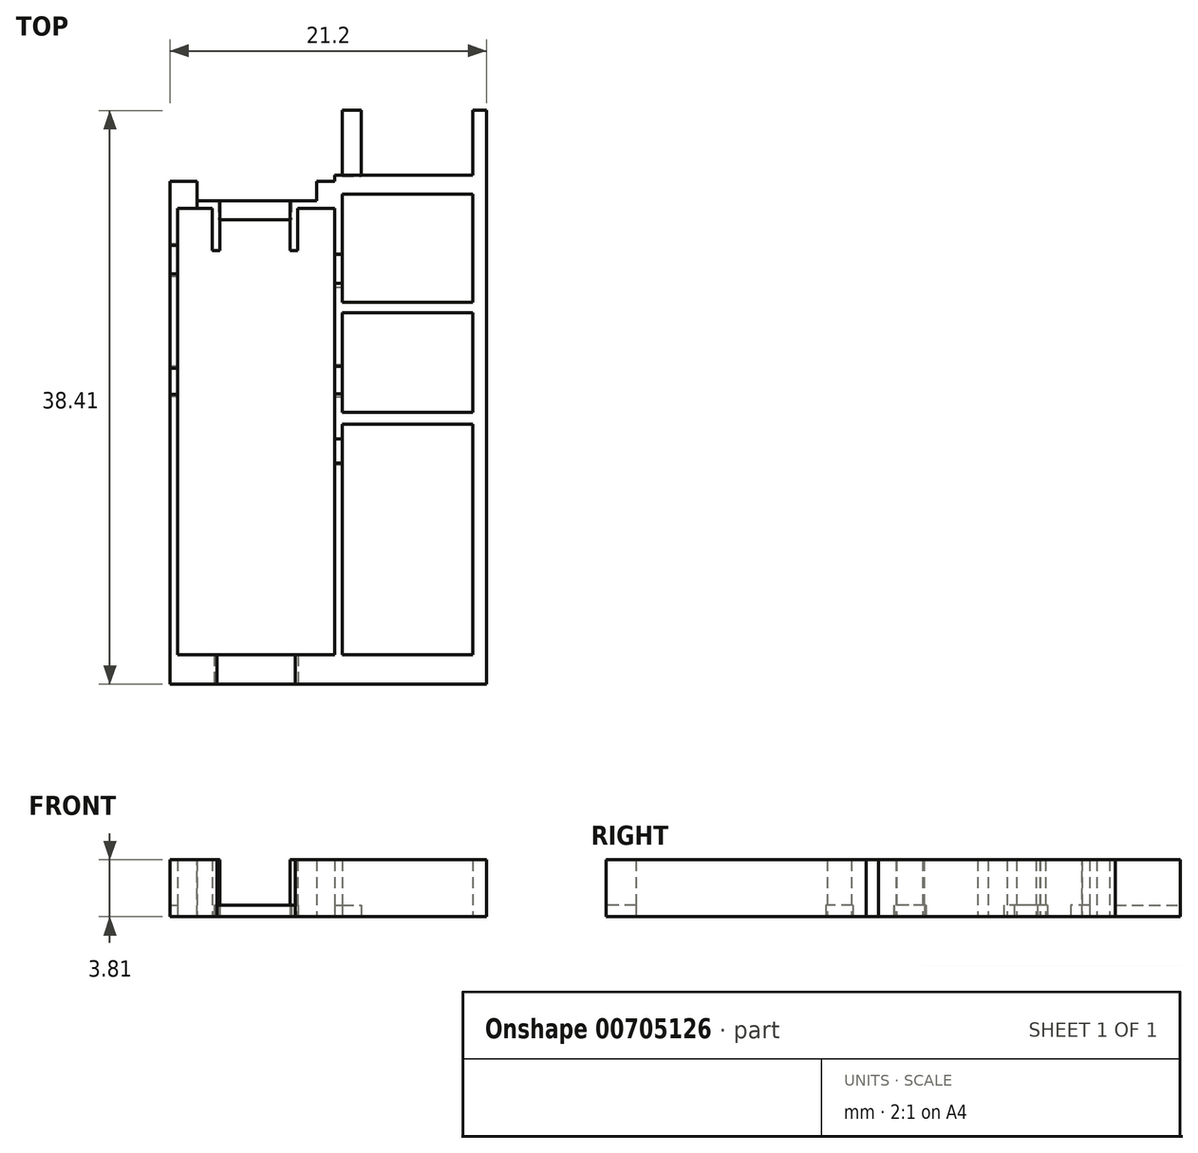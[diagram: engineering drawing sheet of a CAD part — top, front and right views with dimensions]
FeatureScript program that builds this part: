
annotation { "Feature Type Name" : "Feature", "Feature Type Description" : "" }
export const myFeature = defineFeature(function(context is Context, id is Id, definition is map)
    precondition{}
    {
        {
            var Q0;
            Q0=qCreatedBy(makeId("Top.planeOp"),FACE);
            var sketch = newSketch(context, id + "F0", { "sketchPlane" : qUnion([Q0])});
            skLineSegment(sketch, "E0.bottom", {"start": v(19.6, -47.44) * mm, "end": v(20.1, -47.44) * mm});
            skLineSegment(sketch, "E0.top", {"start": v(19.6, -42.13) * mm, "end": v(20.1, -42.13) * mm});
            skLineSegment(sketch, "E0.left", {"start": v(19.6, -47.44) * mm, "end": v(19.6, -42.13) * mm});
            skLineSegment(sketch, "E0.right", {"start": v(20.1, -47.44) * mm, "end": v(20.1, -42.13) * mm});
            skLineSegment(sketch, "E1.bottom", {"start": v(19.6, -49.37) * mm, "end": v(20.1, -49.37) * mm});
            skLineSegment(sketch, "E1.top", {"start": v(19.6, -54.93) * mm, "end": v(20.1, -54.93) * mm});
            skLineSegment(sketch, "E1.left", {"start": v(19.6, -49.37) * mm, "end": v(19.6, -54.93) * mm});
            skLineSegment(sketch, "E1.right", {"start": v(20.1, -49.37) * mm, "end": v(20.1, -54.93) * mm});
            skLineSegment(sketch, "E2.bottom", {"start": v(19.6, -61.4) * mm, "end": v(20.1, -61.4) * mm});
            skLineSegment(sketch, "E2.top", {"start": v(19.6, -74.22) * mm, "end": v(20.1, -74.22) * mm});
            skLineSegment(sketch, "E2.left", {"start": v(19.6, -61.4) * mm, "end": v(19.6, -74.22) * mm});
            skLineSegment(sketch, "E2.right", {"start": v(20.1, -61.4) * mm, "end": v(20.1, -74.22) * mm});
            skLineSegment(sketch, "E3.bottom", {"start": v(19.6, -56.76) * mm, "end": v(20.1, -56.76) * mm});
            skLineSegment(sketch, "E3.top", {"start": v(19.6, -59.79) * mm, "end": v(20.1, -59.79) * mm});
            skLineSegment(sketch, "E3.left", {"start": v(19.6, -56.76) * mm, "end": v(19.6, -59.79) * mm});
            skLineSegment(sketch, "E3.right", {"start": v(20.1, -56.76) * mm, "end": v(20.1, -59.79) * mm});
            skLineSegment(sketch, "E4.bottom", {"start": v(20.1, -58) * mm, "end": v(29.76, -58) * mm});
            skLineSegment(sketch, "E4.top", {"start": v(20.1, -58.8) * mm, "end": v(29.76, -58.8) * mm});
            skLineSegment(sketch, "E4.left", {"start": v(20.1, -58) * mm, "end": v(20.1, -58.8) * mm});
            skLineSegment(sketch, "E4.right", {"start": v(29.76, -58) * mm, "end": v(29.76, -58.8) * mm});
            skLineSegment(sketch, "E5.bottom", {"start": v(20.1, -50.64) * mm, "end": v(29.58, -50.64) * mm});
            skLineSegment(sketch, "E5.top", {"start": v(20.1, -51.34) * mm, "end": v(29.58, -51.34) * mm});
            skLineSegment(sketch, "E5.left", {"start": v(20.1, -50.64) * mm, "end": v(20.1, -51.34) * mm});
            skLineSegment(sketch, "E5.right", {"start": v(29.58, -50.64) * mm, "end": v(29.58, -51.34) * mm});
            skLineSegment(sketch, "E6.bottom", {"start": v(20.1, -42.13) * mm, "end": v(29.74, -42.13) * mm});
            skLineSegment(sketch, "E6.top", {"start": v(20.1, -43.4) * mm, "end": v(29.74, -43.4) * mm});
            skLineSegment(sketch, "E6.left", {"start": v(20.1, -42.13) * mm, "end": v(20.1, -43.4) * mm});
            skLineSegment(sketch, "E6.right", {"start": v(29.74, -42.13) * mm, "end": v(29.74, -43.4) * mm});
            skLineSegment(sketch, "E7.bottom", {"start": v(9.07, -56.8) * mm, "end": v(8.56, -56.8) * mm});
            skLineSegment(sketch, "E7.top", {"start": v(9.07, -74.23) * mm, "end": v(8.56, -74.23) * mm});
            skLineSegment(sketch, "E7.left", {"start": v(9.07, -56.8) * mm, "end": v(9.07, -74.23) * mm});
            skLineSegment(sketch, "E7.right", {"start": v(8.56, -56.8) * mm, "end": v(8.56, -74.23) * mm});
            skLineSegment(sketch, "E8.bottom", {"start": v(9.07, -55.04) * mm, "end": v(8.56, -55.04) * mm});
            skLineSegment(sketch, "E8.top", {"start": v(9.07, -48.74) * mm, "end": v(8.56, -48.74) * mm});
            skLineSegment(sketch, "E8.left", {"start": v(9.07, -55.04) * mm, "end": v(9.07, -48.74) * mm});
            skLineSegment(sketch, "E8.right", {"start": v(8.56, -55.04) * mm, "end": v(8.56, -48.74) * mm});
            skLineSegment(sketch, "E9.bottom", {"start": v(8.57, -42.53) * mm, "end": v(10.38, -42.53) * mm});
            skLineSegment(sketch, "E9.top", {"start": v(8.57, -44.35) * mm, "end": v(10.38, -44.35) * mm});
            skLineSegment(sketch, "E9.left", {"start": v(8.57, -42.53) * mm, "end": v(8.57, -44.35) * mm});
            skLineSegment(sketch, "E9.right", {"start": v(10.38, -42.53) * mm, "end": v(10.38, -44.35) * mm});
            skLineSegment(sketch, "E10.bottom", {"start": v(8.57, -44.35) * mm, "end": v(9.08, -44.35) * mm});
            skLineSegment(sketch, "E10.top", {"start": v(8.57, -46.82) * mm, "end": v(9.08, -46.82) * mm});
            skLineSegment(sketch, "E10.left", {"start": v(8.57, -44.35) * mm, "end": v(8.57, -46.82) * mm});
            skLineSegment(sketch, "E10.right", {"start": v(9.08, -44.35) * mm, "end": v(9.08, -46.82) * mm});
            skLineSegment(sketch, "E11.bottom", {"start": v(10.38, -44.35) * mm, "end": v(11.41, -44.35) * mm});
            skLineSegment(sketch, "E11.top", {"start": v(10.38, -43.84) * mm, "end": v(11.41, -43.84) * mm});
            skLineSegment(sketch, "E11.left", {"start": v(10.38, -44.35) * mm, "end": v(10.38, -43.84) * mm});
            skLineSegment(sketch, "E11.right", {"start": v(11.41, -44.35) * mm, "end": v(11.41, -43.84) * mm});
            skLineSegment(sketch, "E12.bottom", {"start": v(11.41, -43.84) * mm, "end": v(11.92, -43.84) * mm});
            skLineSegment(sketch, "E12.top", {"start": v(11.41, -47.17) * mm, "end": v(11.92, -47.17) * mm});
            skLineSegment(sketch, "E12.left", {"start": v(11.41, -43.84) * mm, "end": v(11.41, -47.17) * mm});
            skLineSegment(sketch, "E12.right", {"start": v(11.92, -43.84) * mm, "end": v(11.92, -47.17) * mm});
            skLineSegment(sketch, "E13.bottom", {"start": v(19.6, -42.53) * mm, "end": v(18.37, -42.53) * mm});
            skLineSegment(sketch, "E13.top", {"start": v(19.6, -44.35) * mm, "end": v(18.37, -44.35) * mm});
            skLineSegment(sketch, "E13.left", {"start": v(19.6, -42.53) * mm, "end": v(19.6, -44.35) * mm});
            skLineSegment(sketch, "E13.right", {"start": v(18.37, -42.53) * mm, "end": v(18.37, -44.35) * mm});
            skLineSegment(sketch, "E14.bottom", {"start": v(18.37, -44.35) * mm, "end": v(17.12, -44.35) * mm});
            skLineSegment(sketch, "E14.top", {"start": v(18.37, -43.84) * mm, "end": v(17.12, -43.84) * mm});
            skLineSegment(sketch, "E14.left", {"start": v(18.37, -44.35) * mm, "end": v(18.37, -43.84) * mm});
            skLineSegment(sketch, "E14.right", {"start": v(17.12, -44.35) * mm, "end": v(17.12, -43.84) * mm});
            skLineSegment(sketch, "E15.bottom", {"start": v(17.12, -43.84) * mm, "end": v(16.6, -43.84) * mm});
            skLineSegment(sketch, "E15.top", {"start": v(17.12, -47.16) * mm, "end": v(16.6, -47.16) * mm});
            skLineSegment(sketch, "E15.left", {"start": v(17.12, -43.84) * mm, "end": v(17.12, -47.16) * mm});
            skLineSegment(sketch, "E15.right", {"start": v(16.6, -43.84) * mm, "end": v(16.6, -47.16) * mm});
            skLineSegment(sketch, "E16.bottom", {"start": v(29.74, -42.13) * mm, "end": v(28.84, -42.13) * mm});
            skLineSegment(sketch, "E16.top", {"start": v(29.74, -76.2) * mm, "end": v(28.84, -76.2) * mm});
            skLineSegment(sketch, "E16.left", {"start": v(29.74, -42.13) * mm, "end": v(29.74, -76.2) * mm});
            skLineSegment(sketch, "E16.right", {"start": v(28.84, -42.13) * mm, "end": v(28.84, -76.2) * mm});
            skLineSegment(sketch, "E17.bottom", {"start": v(28.84, -76.2) * mm, "end": v(16.95, -76.2) * mm});
            skLineSegment(sketch, "E17.top", {"start": v(28.84, -74.22) * mm, "end": v(16.95, -74.22) * mm});
            skLineSegment(sketch, "E17.left", {"start": v(28.84, -76.2) * mm, "end": v(28.84, -74.22) * mm});
            skLineSegment(sketch, "E17.right", {"start": v(16.95, -76.2) * mm, "end": v(16.95, -74.22) * mm});
            skLineSegment(sketch, "E18.bottom", {"start": v(11.71, -76.2) * mm, "end": v(8.56, -76.2) * mm});
            skLineSegment(sketch, "E18.top", {"start": v(11.71, -74.22) * mm, "end": v(8.56, -74.22) * mm});
            skLineSegment(sketch, "E18.left", {"start": v(11.71, -76.2) * mm, "end": v(11.71, -74.22) * mm});
            skLineSegment(sketch, "E18.right", {"start": v(8.56, -76.2) * mm, "end": v(8.56, -74.22) * mm});
            skLineSegment(sketch, "E19.top", {"start": v(29.75, -42.13) * mm, "end": v(28.84, -42.13) * mm});
            skLineSegment(sketch, "E19.left", {"start": v(29.75, -37.79) * mm, "end": v(29.75, -42.13) * mm});
            skLineSegment(sketch, "E19.right", {"start": v(28.84, -37.79) * mm, "end": v(28.84, -42.13) * mm});
            skLineSegment(sketch, "E20", {"start": v(28.84, -37.79) * mm, "end": v(29.75, -37.79) * mm});
            skPoint(sketch, "E21.endSnap0", {"position": v(22.9, -76.2) * mm});
            skLineSegment(sketch, "E22", {"start": v(8.56, -76.2) * mm, "end": v(29.74, -76.2) * mm});
            skSolve(sketch);
        }
        {
            var Q0;
            Q0=qSketchRegion(id+"F0",true);
            extrude(context, id + "F1", {"entities" : qUnion([Q0]), "depth" : 3.8 * mm, "offsetDistance" : 25.4 * mm});
        }
        {
            var Q0;
            Q0=qCreatedBy(makeId("Top.planeOp"),FACE);
            var sketch = newSketch(context, id + "F2", { "sketchPlane" : qUnion([Q0])});
            skLineSegment(sketch, "E23.bottom", {"start": v(11.81, -43.84) * mm, "end": v(16.72, -43.84) * mm});
            skLineSegment(sketch, "E23.top", {"start": v(11.81, -45.11) * mm, "end": v(16.72, -45.11) * mm});
            skLineSegment(sketch, "E23.left", {"start": v(11.81, -43.84) * mm, "end": v(11.81, -45.11) * mm});
            skLineSegment(sketch, "E23.right", {"start": v(16.72, -43.84) * mm, "end": v(16.72, -45.11) * mm});
            skLineSegment(sketch, "E24.bottom", {"start": v(19.6, -54.8) * mm, "end": v(20.1, -54.8) * mm});
            skLineSegment(sketch, "E24.top", {"start": v(19.6, -56.96) * mm, "end": v(20.1, -56.96) * mm});
            skLineSegment(sketch, "E24.left", {"start": v(19.6, -54.8) * mm, "end": v(19.6, -56.96) * mm});
            skLineSegment(sketch, "E24.right", {"start": v(20.1, -54.8) * mm, "end": v(20.1, -56.96) * mm});
            skLineSegment(sketch, "E25.bottom", {"start": v(11.53, -74.21) * mm, "end": v(17.14, -74.21) * mm});
            skLineSegment(sketch, "E25.top", {"start": v(11.53, -76.2) * mm, "end": v(17.14, -76.2) * mm});
            skLineSegment(sketch, "E25.left", {"start": v(11.53, -74.21) * mm, "end": v(11.53, -76.2) * mm});
            skLineSegment(sketch, "E25.right", {"start": v(17.14, -74.21) * mm, "end": v(17.14, -76.2) * mm});
            skLineSegment(sketch, "E26.bottom", {"start": v(19.6, -59.7) * mm, "end": v(20.1, -59.7) * mm});
            skLineSegment(sketch, "E26.top", {"start": v(19.6, -61.5) * mm, "end": v(20.1, -61.5) * mm});
            skLineSegment(sketch, "E26.left", {"start": v(19.6, -59.7) * mm, "end": v(19.6, -61.5) * mm});
            skLineSegment(sketch, "E26.right", {"start": v(20.1, -59.7) * mm, "end": v(20.1, -61.5) * mm});
            skLineSegment(sketch, "E27.bottom", {"start": v(8.56, -56.93) * mm, "end": v(9.07, -56.93) * mm});
            skLineSegment(sketch, "E27.top", {"start": v(8.56, -54.89) * mm, "end": v(9.07, -54.89) * mm});
            skLineSegment(sketch, "E27.left", {"start": v(8.56, -54.89) * mm, "end": v(8.56, -56.93) * mm});
            skLineSegment(sketch, "E27.right", {"start": v(9.07, -54.89) * mm, "end": v(9.07, -56.93) * mm});
            skLineSegment(sketch, "E28.bottom", {"start": v(19.6, -47.33) * mm, "end": v(20.1, -47.33) * mm});
            skLineSegment(sketch, "E28.top", {"start": v(19.6, -49.6) * mm, "end": v(20.1, -49.6) * mm});
            skLineSegment(sketch, "E28.left", {"start": v(19.6, -47.33) * mm, "end": v(19.6, -49.6) * mm});
            skLineSegment(sketch, "E28.right", {"start": v(20.1, -47.33) * mm, "end": v(20.1, -49.6) * mm});
            skLineSegment(sketch, "E29.bottom", {"start": v(8.56, -46.69) * mm, "end": v(9.07, -46.69) * mm});
            skLineSegment(sketch, "E29.top", {"start": v(8.56, -48.9) * mm, "end": v(9.07, -48.9) * mm});
            skLineSegment(sketch, "E29.left", {"start": v(8.56, -46.69) * mm, "end": v(8.56, -48.9) * mm});
            skLineSegment(sketch, "E29.right", {"start": v(9.07, -46.69) * mm, "end": v(9.07, -48.9) * mm});
            skLineSegment(sketch, "E30.bottom", {"start": v(20.1, -42.17) * mm, "end": v(21.37, -42.17) * mm});
            skLineSegment(sketch, "E30.top", {"start": v(20.1, -37.79) * mm, "end": v(21.37, -37.79) * mm});
            skLineSegment(sketch, "E30.left", {"start": v(20.1, -42.17) * mm, "end": v(20.1, -37.79) * mm});
            skLineSegment(sketch, "E30.right", {"start": v(21.37, -42.17) * mm, "end": v(21.37, -37.79) * mm});
            skSolve(sketch);
        }
        {
            var Q0;
            Q0 = qSketchRegion(id + "F2", true);
            extrude(context, id + "F3", {"entities" : qUnion([Q0]), "depth" : 0.76 * mm, "offsetDistance" : 25.4 * mm});
        }
    });
